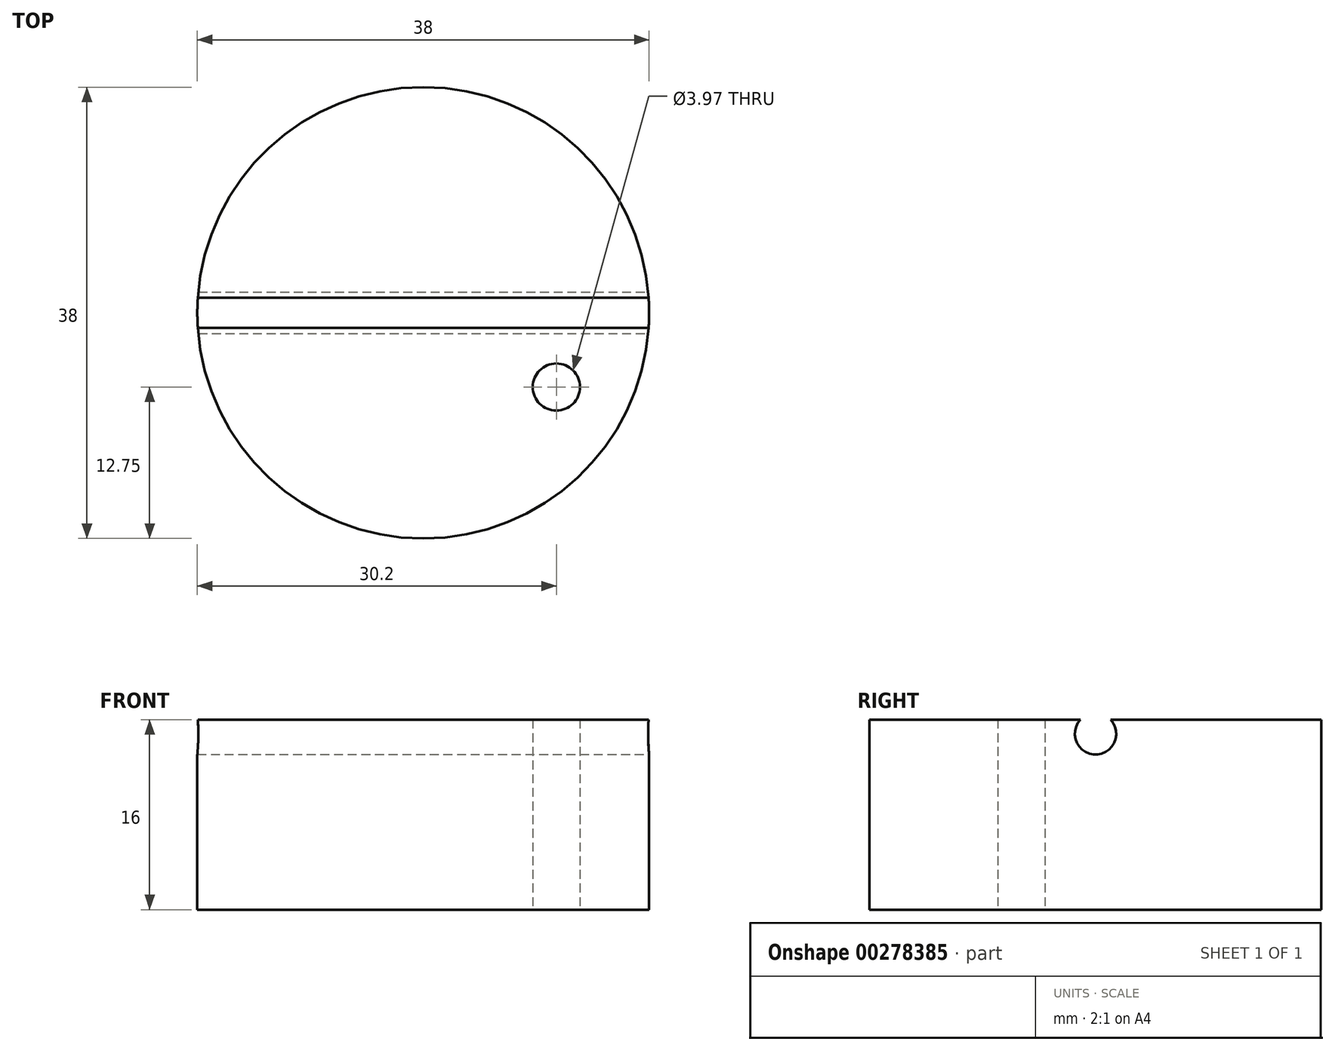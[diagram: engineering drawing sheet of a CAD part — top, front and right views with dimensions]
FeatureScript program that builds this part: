
annotation { "Feature Type Name" : "Feature", "Feature Type Description" : "" }
export const myFeature = defineFeature(function(context is Context, id is Id, definition is map)
    precondition{}
    {
        {
            var Q0;
            Q0=qCreatedBy(makeId("Top.planeOp"),FACE);
            var sketch = newSketch(context, id + "F0", { "sketchPlane" : qUnion([Q0])});
            skCircle(sketch, "E0", {"center": v(0, 0) * mm, "radius": 19 * mm});
            skSolve(sketch);
        }
        {
            var Q0;
            Q0=makeQuery(id+"F0.imprint","IMPRINT",FACE,{"disambiguationData":[TD([[makeQuery(id+"F0.imprint","IMPRINT",EDGE,{"derivedFrom":sQuery(id+"F0.wireOp",EDGE,"E0")}),1.0]])]});
            extrude(context, id + "F1", {"entities" : qUnion([Q0]), "depth" : 16 * mm});
        }
        {
            var Q0;
            Q0=qCreatedBy(makeId("Right.planeOp"),FACE);
            var sketch = newSketch(context, id + "F2", { "sketchPlane" : qUnion([Q0])});
            skCircle(sketch, "E1", {"center": v(0, 14.8) * mm, "radius": 1.74 * mm});
            skSolve(sketch);
        }
        {
            var Q0;
            Q0 = qSketchRegion(id + "F2", true);
            extrude(context, id + "F3", {"entities" : qUnion([Q0]), "operationType" : NewBodyOperationType.REMOVE, "endBound" : BoundingType.THROUGH_ALL, "oppositeDirection" : true, "depth" : 25 * mm, "hasSecondDirection" : true, "secondDirectionBound" : SecondDirectionBoundingType.THROUGH_ALL, "secondDirectionOppositeDirection" : false, "secondDirectionDepth" : 25 * mm});
        }
        {
            var Q0;
            Q0=qCreatedBy(makeId("Top.planeOp"),FACE);
            var sketch = newSketch(context, id + "F4", { "sketchPlane" : qUnion([Q0])});
            skCircle(sketch, "E2", {"center": v(11.2, -6.25) * mm, "radius": 1.98 * mm});
            skCircle(sketch, "E3.MirrorC", {"center": v(11.2, 6.25) * mm, "radius": 1.98 * mm});
            skSolve(sketch);
        }
        {
            var Q0;
            Q0=makeQuery(id+"F4.imprint","IMPRINT",FACE,{"disambiguationData":[TD([[makeQuery(id+"F4.imprint","IMPRINT",EDGE,{"derivedFrom":sQuery(id+"F4.wireOp",EDGE,"E2")}),1.0]])]});
            var Q1;
            Q1=makeQuery(id+"F4.imprint","IMPRINT",FACE,{"disambiguationData":[TD([[makeQuery(id+"F4.imprint","IMPRINT",EDGE,{"derivedFrom":sQuery(id+"F4.wireOp",EDGE,"E3.MirrorC")}),-1.0]])]});
            extrude(context, id + "F5", {"entities" : qUnion([Q0, Q1]), "operationType" : NewBodyOperationType.REMOVE, "endBound" : BoundingType.THROUGH_ALL, "depth" : 25 * mm});
        }
    });
